# Revit family: P_Trap-DXV-Decorative-D35700020_Series
name_source: partatom
category: Plumbing Fixtures
units: mm (PartAtom-declared; Revit-internal decimal feet)

## family parameters
Cut with Voids When Loaded = No
Host = Face
OmniClass Number = 23.45.55.21
OmniClass Title = Drains (Wastes)
Part Type = Normal
Room Calculation Point = No
Round Connector Dimension = Use Radius
Shared = Yes

## types (5) — shared parameters
ASME A112.18.1/CSA B125.1 = Yes
Assembly Code = D2030100
CW Connection = No
Default Elevation = 0"
Description = Decorative P-Trap
HW Connection = No
Height = 7 3/8"
Installation Type = Wall Mounted
Length = 15 7/16"
Manufacturer = DXV
Price = Prices may vary. Please consult Manufacturer Representative for most up-to-date price list.
Product Documentation Link = https://dxv01.blob.core.windows.net
Product Page URL = https://www.dxv.com
Revised Date = 02/08/2022
URL = http://www.dxv.com
Vent Connection = No
WFU = 2
Warranty Documentation Link = https://www.dxv.com
Waste Connection = Yes
Waste Connection Diameter = 1 1/4"
Waste Connection Radius = 5/8"
Width = 2 5/8"
zero-valued in all types: CWFU, HWFU

## per-type parameters (varying)
| type | Finish | Material |
| D35700020.110 | Metal-DXV-110-Carbon Bronze | Metal-DXV-110-Carbon Bronze |
| D35700020.144 | Metal-DXV-144-Brushed Nickel | Metal-DXV-144-Brushed Nickel |
| D35700020.100 | Metal-DXV-100-Polished Chrome | Metal-DXV-100-Polished Chrome |
| D35700020.150 | Metal-DXV-150-Platinum Nickel | Metal-DXV-150-Platinum Nickel |
| D35700020.427 | Metal-DXV-427-Satin Brass | Metal-DXV-427-Satin Brass |

note: column(s) folded — value = type name in every type: Model

## geometry (parser evidence)
native form markers: Sweep x3
no freeform markers — native parametric forms only
